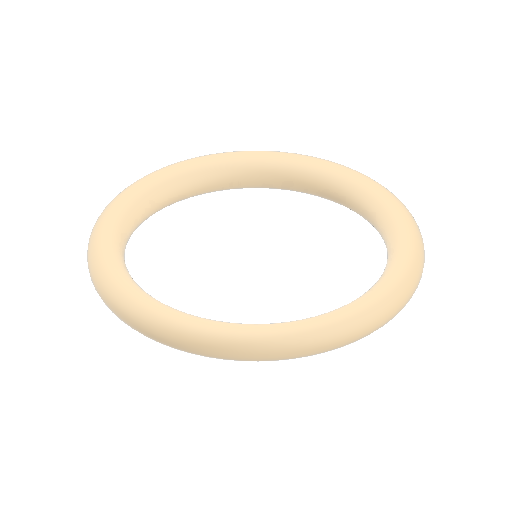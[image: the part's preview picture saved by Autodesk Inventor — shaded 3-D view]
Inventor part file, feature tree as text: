
AUTODESK INVENTOR PART (.ipt)
format: ipt  version: 2024.3 (Build 283343000, 343)  size: 279,552 bytes
history: native  units: mm
features: revolve x1, sketch x1
ambient origin geometry x8: Origin, YZ Plane, XZ Plane, XY Plane, X Axis, Y Axis, Z Axis, Center Point
bodies: Solid1 (feature_tree)
feature tree (2):
  revolve  "Revolution1"  [1 undecoded]
  sketch  "Sketch3"  dims[d3=0.5mm d4=2.0mm d5=90.0deg]
note: 1 required parameter value undecoded (feature->parameter linkage not recoverable at this tier; creation-order binding heuristic only, values carry confidence <= 0.55)
